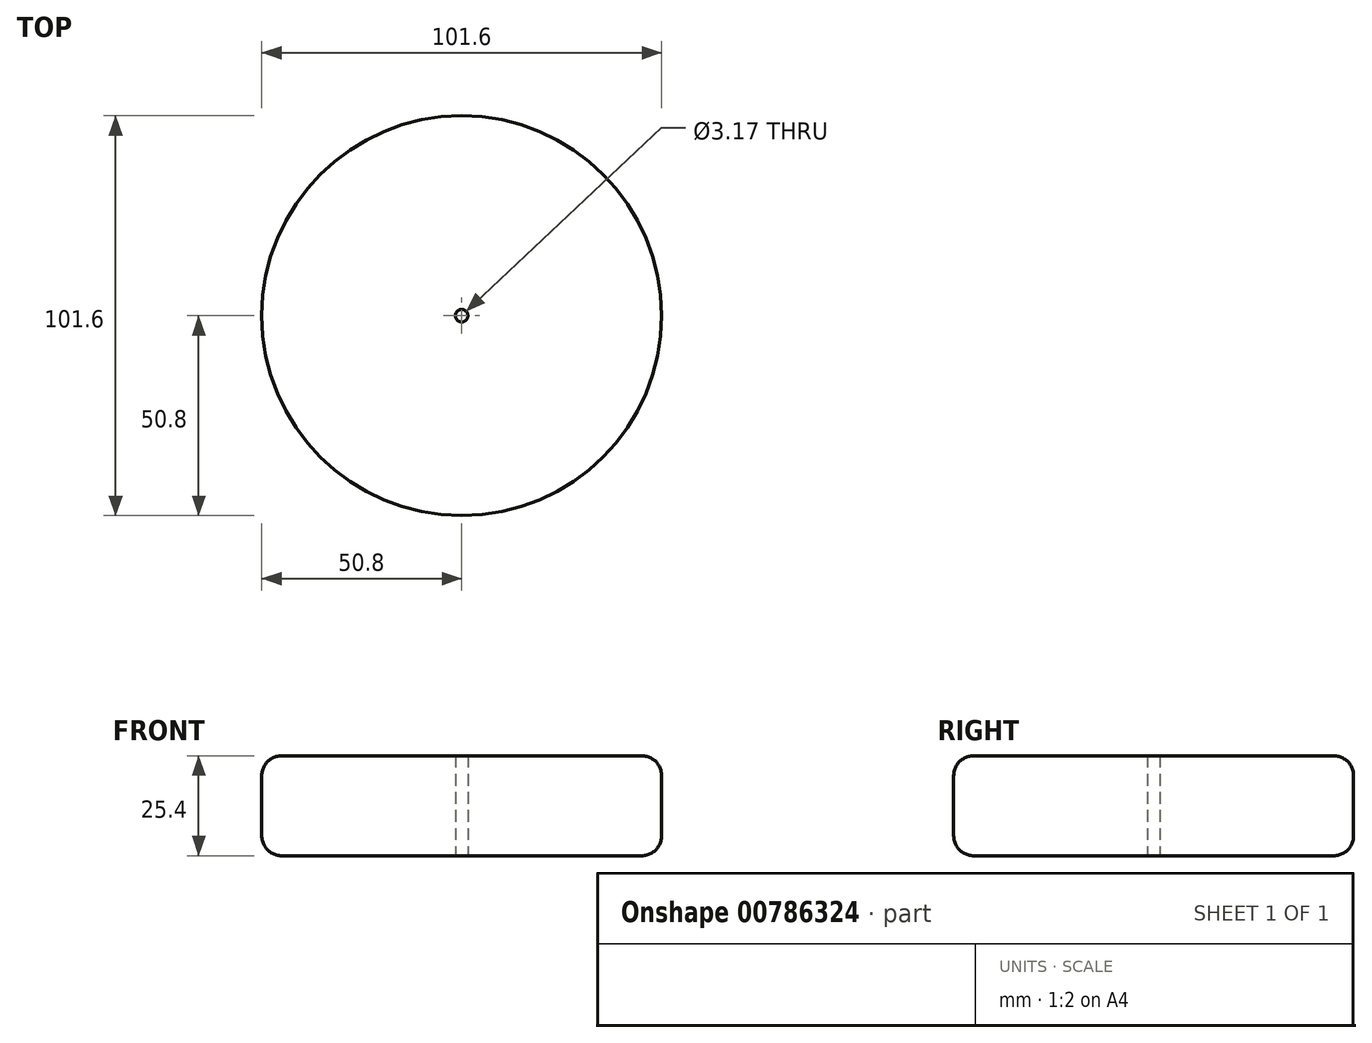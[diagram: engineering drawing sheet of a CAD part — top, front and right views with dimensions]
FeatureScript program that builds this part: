
annotation { "Feature Type Name" : "Feature", "Feature Type Description" : "" }
export const myFeature = defineFeature(function(context is Context, id is Id, definition is map)
    precondition{}
    {
        {
            var Q0;
            Q0=qCreatedBy(makeId("Top.planeOp"),FACE);
            var sketch = newSketch(context, id + "F0", { "sketchPlane" : qUnion([Q0])});
            skCircle(sketch, "E0", {"center": v(0, 0) * mm, "radius": 50.8 * mm});
            skCircle(sketch, "E1", {"center": v(0, 0) * mm, "radius": 1.59 * mm});
            skSolve(sketch);
        }
        {
            var Q0;
            Q0 = qSketchRegion(id + "F0", true);
            extrude(context, id + "F1", {"entities" : qUnion([Q0]), "depth" : 25.4 * mm, "offsetDistance" : 25.4 * mm});
        }
        {
            var Q0;
            Q0=makeQuery(id+"F0.imprint","IMPRINT",FACE,{"disambiguationData":[TD([[makeQuery(id+"F0.imprint","IMPRINT",EDGE,{"derivedFrom":sQuery(id+"F0.wireOp",EDGE,"E0")}),1.0]])]});
            extrude(context, id + "F2", {"entities" : qUnion([Q0]), "operationType" : NewBodyOperationType.ADD, "depth" : 25.4 * mm, "offsetDistance" : 25.4 * mm});
        }
        {
            var Q0;
            Q0=makeQuery(id+"F1.opExtrude","CAP_EDGE",EDGE,{"disambiguationData":[OSD([sQuery(id+"F0.wireOp",EDGE,"E0")])],"isStart":true});
            var Q1;
            Q1=makeQuery(id+"F1.opExtrude","SWEPT_FACE",FACE,{"disambiguationData":[OSD([sQuery(id+"F0.wireOp",EDGE,"E0")])]});
            fillet(context, id + "F3", {"entities" : qUnion([Q0, Q1]), "radius" : 5.08 * mm, "tangentPropagation" : true, "allowEdgeOverflow" : false});
        }
    });
